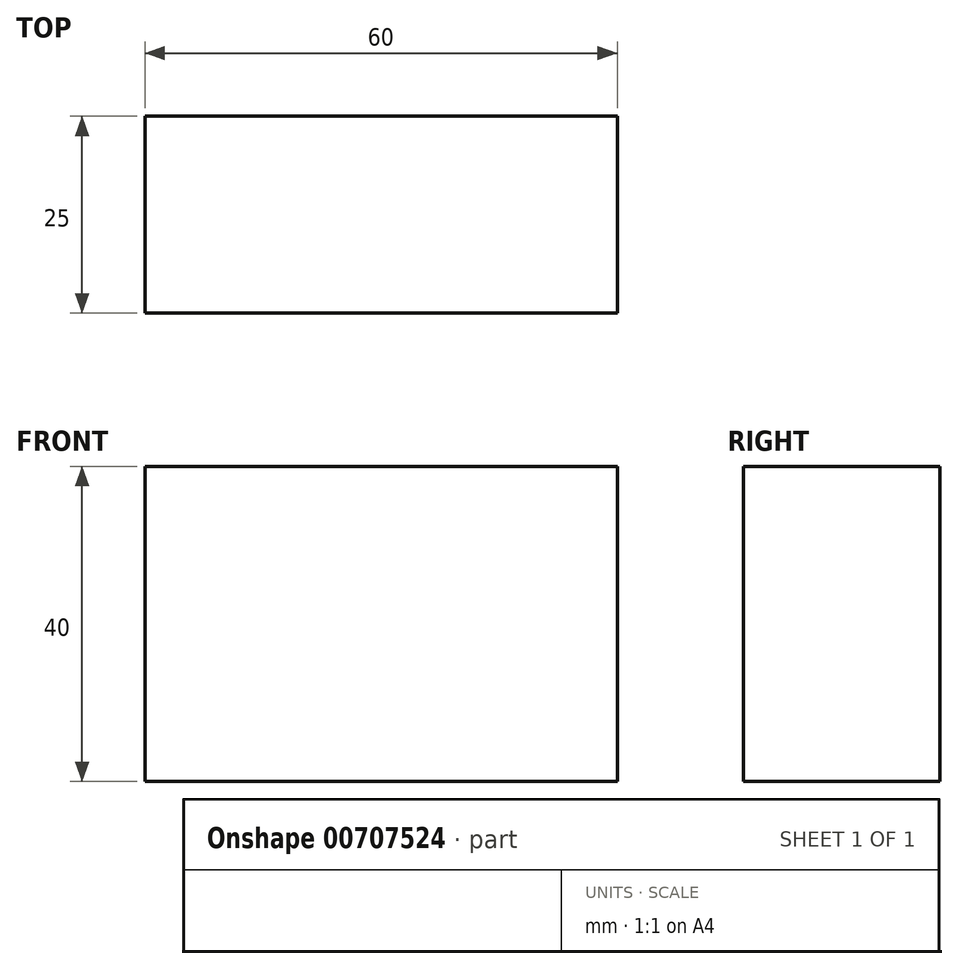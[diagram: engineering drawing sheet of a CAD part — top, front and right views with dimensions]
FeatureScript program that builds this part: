
annotation { "Feature Type Name" : "Feature", "Feature Type Description" : "" }
export const myFeature = defineFeature(function(context is Context, id is Id, definition is map)
    precondition{}
    {
        {
            var Q0;
            Q0=qCreatedBy(makeId("Front.planeOp"),FACE);
            var sketch = newSketch(context, id + "F0", { "sketchPlane" : qUnion([Q0])});
            skLineSegment(sketch, "E0.bottom", {"start": v(0, 0) * mm, "end": v(60, 0) * mm});
            skLineSegment(sketch, "E0.top", {"start": v(0, 40) * mm, "end": v(60, 40) * mm});
            skLineSegment(sketch, "E0.left", {"start": v(0, 0) * mm, "end": v(0, 40) * mm});
            skLineSegment(sketch, "E0.right", {"start": v(60, 0) * mm, "end": v(60, 40) * mm});
            skSolve(sketch);
        }
        {
            var Q0;
            Q0 = qSketchRegion(id + "F0", true);
            extrude(context, id + "F1", {"entities" : qUnion([Q0]), "depth" : 25 * mm, "offsetDistance" : 25 * mm});
        }
    });
